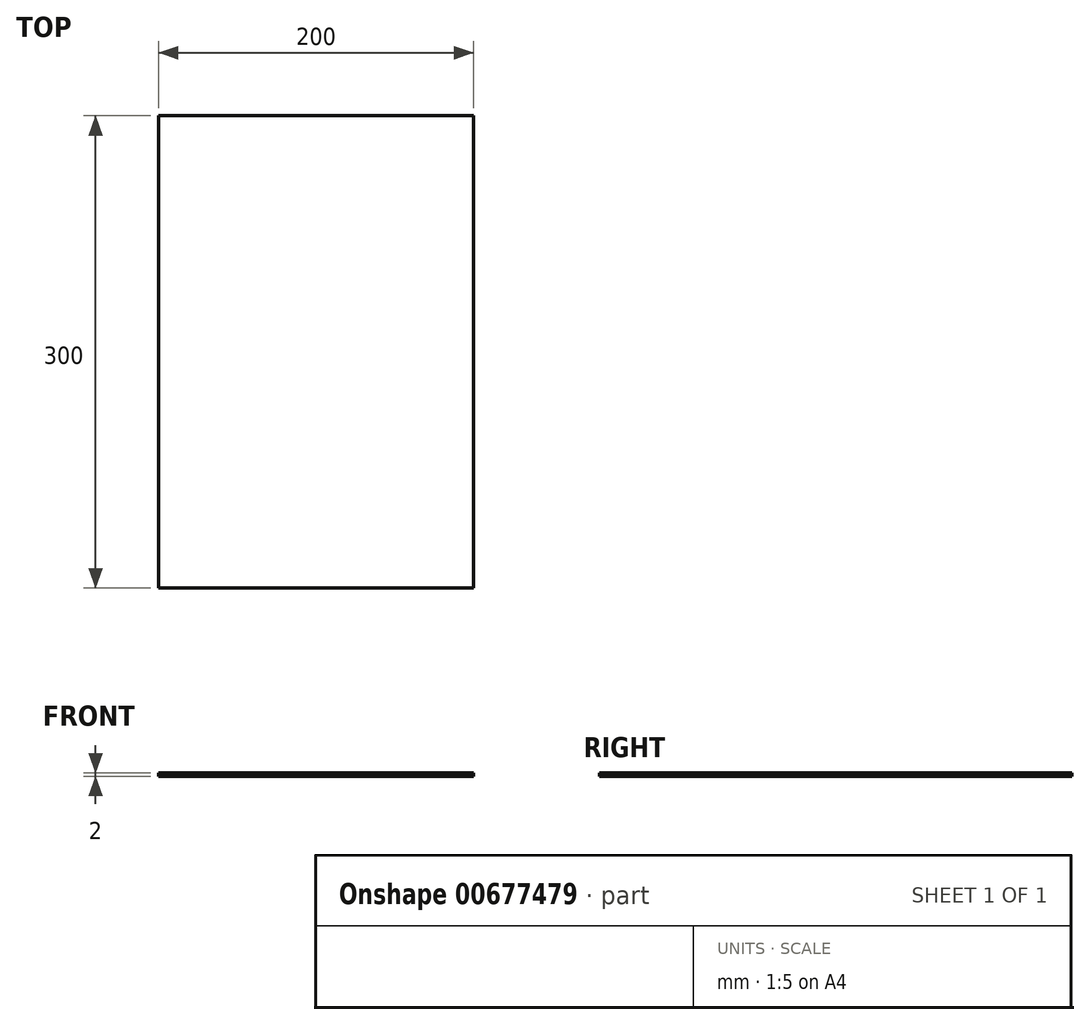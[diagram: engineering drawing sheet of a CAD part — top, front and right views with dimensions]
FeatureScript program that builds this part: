
annotation { "Feature Type Name" : "Feature", "Feature Type Description" : "" }
export const myFeature = defineFeature(function(context is Context, id is Id, definition is map)
    precondition{}
    {
        {
            var Q0;
            Q0=qCreatedBy(makeId("Top.planeOp"),FACE);
            var sketch = newSketch(context, id + "F0", { "sketchPlane" : qUnion([Q0])});
            skLineSegment(sketch, "E0.bottom", {"start": v(-100, 150) * mm, "end": v(100, 150) * mm});
            skLineSegment(sketch, "E0.top", {"start": v(-100, -150) * mm, "end": v(100, -150) * mm});
            skLineSegment(sketch, "E0.left", {"start": v(-100, 150) * mm, "end": v(-100, -150) * mm});
            skLineSegment(sketch, "E0.right", {"start": v(100, 150) * mm, "end": v(100, -150) * mm});
            skPoint(sketch, "E0.middle", {"position": v(0, 0) * mm});
            skSolve(sketch);
        }
        {
            var Q0;
            Q0 = qSketchRegion(id + "F0", true);
            extrude(context, id + "F1", {"entities" : qUnion([Q0]), "depth" : 2 * mm, "offsetDistance" : 25 * mm});
        }
    });
